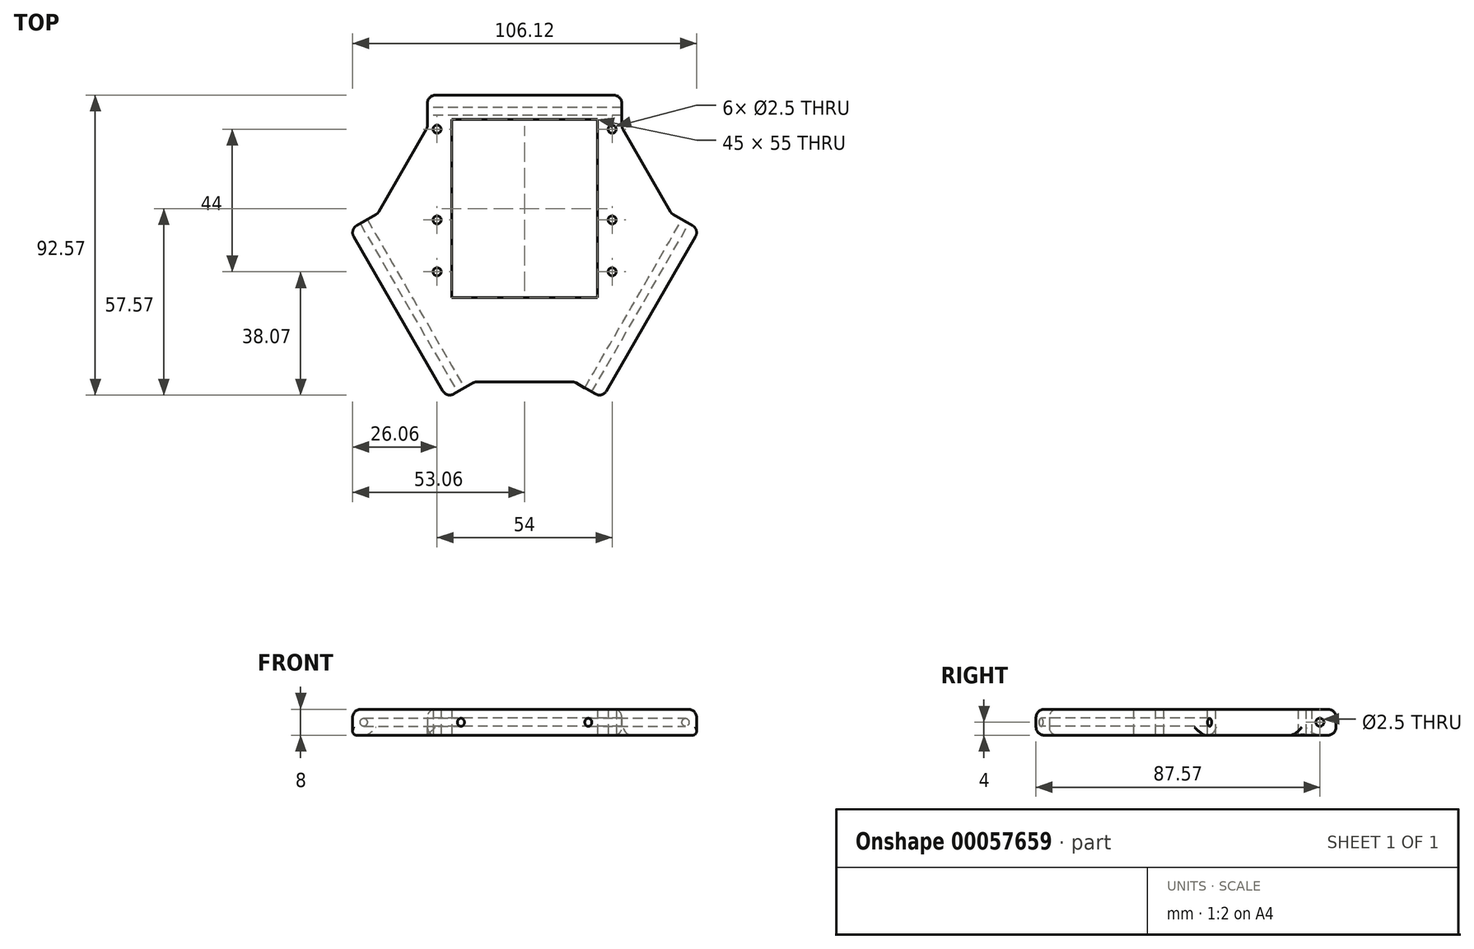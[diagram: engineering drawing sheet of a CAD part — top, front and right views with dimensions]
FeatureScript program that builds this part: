
annotation { "Feature Type Name" : "Feature", "Feature Type Description" : "" }
export const myFeature = defineFeature(function(context is Context, id is Id, definition is map)
    precondition{}
    {
        {
            var Q0;
            Q0=qCreatedBy(makeId("Top.planeOp"),FACE);
            var sketch = newSketch(context, id + "F0", { "sketchPlane" : qUnion([Q0])});
            skLineSegment(sketch, "E0", {"start": v(0, 0) * mm, "end": v(0, 78.7) * mm, "construction": true});
            skLineSegment(sketch, "E1", {"start": v(0, 0) * mm, "end": v(-104.2, -60.16) * mm, "construction": true});
            skLineSegment(sketch, "E2", {"start": v(0, 0) * mm, "end": v(103.59, -59.8) * mm, "construction": true});
            skLineSegment(sketch, "E3.bottom", {"start": v(-30, 45) * mm, "end": v(30, 45) * mm});
            skLineSegment(sketch, "E3.top", {"start": v(-30, 35) * mm, "end": v(30, 35) * mm});
            skLineSegment(sketch, "E3.left", {"start": v(-30, 45) * mm, "end": v(-30, 35) * mm});
            skLineSegment(sketch, "E3.right", {"start": v(30, 45) * mm, "end": v(30, 35) * mm});
            skPoint(sketch, "E4", {"position": v(0, 35) * mm});
            skPoint(sketch, "E5", {"position": v(0, 0) * mm});
            skLineSegment(sketch, "E6.rect.bottom", {"start": v(22.5, -17.5) * mm, "end": v(-22.5, -17.5) * mm});
            skLineSegment(sketch, "E6.rect.top", {"start": v(22.5, 17.5) * mm, "end": v(-22.5, 17.5) * mm});
            skLineSegment(sketch, "E6.rect.left", {"start": v(22.5, -17.5) * mm, "end": v(22.5, 17.5) * mm});
            skLineSegment(sketch, "E6.rect.right", {"start": v(-22.5, -17.5) * mm, "end": v(-22.5, 17.5) * mm});
            skLineSegment(sketch, "E7.1.0", {"start": v(-23.97, -48.48) * mm, "end": v(-53.97, 3.48) * mm});
            skLineSegment(sketch, "E7.1.1", {"start": v(-15.31, -43.48) * mm, "end": v(-45.31, 8.48) * mm});
            skLineSegment(sketch, "E7.1.2", {"start": v(-53.97, 3.48) * mm, "end": v(-45.31, 8.48) * mm});
            skLineSegment(sketch, "E7.1.3", {"start": v(-23.97, -48.48) * mm, "end": v(-15.31, -43.48) * mm});
            skLineSegment(sketch, "E7.2.0", {"start": v(53.97, 3.48) * mm, "end": v(23.97, -48.48) * mm});
            skLineSegment(sketch, "E7.2.1", {"start": v(45.31, 8.48) * mm, "end": v(15.31, -43.48) * mm});
            skLineSegment(sketch, "E7.2.2", {"start": v(23.97, -48.48) * mm, "end": v(15.31, -43.48) * mm});
            skLineSegment(sketch, "E7.2.3", {"start": v(53.97, 3.48) * mm, "end": v(45.31, 8.48) * mm});
            skLineSegment(sketch, "E8", {"start": v(-45.31, 8.48) * mm, "end": v(-30, 35) * mm});
            skLineSegment(sketch, "E9", {"start": v(30, 35) * mm, "end": v(45.31, 8.48) * mm});
            skLineSegment(sketch, "E10", {"start": v(15.31, -43.48) * mm, "end": v(-15.31, -43.48) * mm});
            skLineSegment(sketch, "E11.bottom", {"start": v(-22.5, 17.5) * mm, "end": v(22.5, 17.5) * mm});
            skLineSegment(sketch, "E11.top", {"start": v(-22.5, 37.5) * mm, "end": v(22.5, 37.5) * mm});
            skLineSegment(sketch, "E11.left", {"start": v(-22.5, 17.5) * mm, "end": v(-22.5, 37.5) * mm});
            skLineSegment(sketch, "E11.right", {"start": v(22.5, 17.5) * mm, "end": v(22.5, 37.5) * mm});
            skPoint(sketch, "E12", {"position": v(-27, -9.5) * mm});
            skPoint(sketch, "E13", {"position": v(-27, 6.5) * mm});
            skPoint(sketch, "E14", {"position": v(27, -9.5) * mm});
            skPoint(sketch, "E15", {"position": v(27, 6.5) * mm});
            skPoint(sketch, "E16", {"position": v(-27, 34.5) * mm});
            skPoint(sketch, "E17", {"position": v(27, 34.5) * mm});
            skLineSegment(sketch, "E18", {"start": v(-27, -9.5) * mm, "end": v(27, -9.5) * mm, "construction": true});
            skPoint(sketch, "E19", {"position": v(0, -9.5) * mm});
            skLineSegment(sketch, "E20", {"start": v(0, 0) * mm, "end": v(0, -52.67) * mm, "construction": true});
            skSolve(sketch);
        }
        {
            var Q0;
            Q0=makeQuery(id+"F0.imprint","IMPRINT",FACE,{"disambiguationData":[TD([[makeQuery(id+"F0.imprint","IMPRINT",EDGE,{"derivedFrom":sQuery(id+"F0.wireOp",EDGE,"E3.top")}),-1.0]])]});
            var Q1;
            Q1=makeQuery(id+"F0.imprint","IMPRINT",FACE,{"disambiguationData":[TD([[makeQuery(id+"F0.imprint","IMPRINT",EDGE,{"derivedFrom":sQuery(id+"F0.wireOp",EDGE,"E7.1.0")}),-1.0]])]});
            var Q2;
            Q2=makeQuery(id+"F0.imprint","IMPRINT",FACE,{"disambiguationData":[TD([[makeQuery(id+"F0.imprint","IMPRINT",EDGE,{"derivedFrom":sQuery(id+"F0.wireOp",EDGE,"E3.bottom")}),-1.0]])]});
            var Q3;
            Q3=makeQuery(id+"F0.imprint","IMPRINT",FACE,{"disambiguationData":[TD([[makeQuery(id+"F0.imprint","IMPRINT",EDGE,{"derivedFrom":sQuery(id+"F0.wireOp",EDGE,"E7.2.0")}),-1.0]])]});
            extrude(context, id + "F1", {"entities" : qUnion([Q0, Q1, Q2, Q3]), "depth" : 8 * mm});
        }
        {
            var Q0;
            Q0=makeQuery(id+"F1.opExtrude","SWEPT_FACE",FACE,{"disambiguationData":[OSD([sQuery(id+"F0.wireOp",EDGE,"E3.left")])]});
            var sketch = newSketch(context, id + "F2", { "sketchPlane" : qUnion([Q0])});
            skPoint(sketch, "E21.0", {"position": v(-45, 0) * mm});
            skPoint(sketch, "E21.1", {"position": v(-45, 8) * mm});
            skPoint(sketch, "E22", {"position": v(-40, 4) * mm});
            skSolve(sketch);
        }
        {
            var Q0;
            Q0=sQuery(id+"F2.wireOp",VERTEX,"E22");
            var Q1;
            Q1=makeQuery(id+"F1.opExtrude","SWEPT_BODY",BODY,{"disambiguationData":[OSD([sQuery(id+"F0.wireOp",EDGE,"E3.bottom"),sQuery(id+"F0.wireOp",EDGE,"E3.left"),sQuery(id+"F0.wireOp",EDGE,"E3.right"),sQuery(id+"F0.wireOp",EDGE,"E6.rect.bottom"),sQuery(id+"F0.wireOp",EDGE,"E6.rect.left"),sQuery(id+"F0.wireOp",EDGE,"E6.rect.right"),sQuery(id+"F0.wireOp",EDGE,"E7.1.0"),sQuery(id+"F0.wireOp",EDGE,"E7.1.2"),sQuery(id+"F0.wireOp",EDGE,"E7.1.3"),sQuery(id+"F0.wireOp",EDGE,"E7.2.0"),sQuery(id+"F0.wireOp",EDGE,"E7.2.2"),sQuery(id+"F0.wireOp",EDGE,"E7.2.3"),sQuery(id+"F0.wireOp",EDGE,"E8"),sQuery(id+"F0.wireOp",EDGE,"E9"),sQuery(id+"F0.wireOp",EDGE,"E10"),sQuery(id+"F0.wireOp",EDGE,"E11.top"),sQuery(id+"F0.wireOp",EDGE,"E11.left"),sQuery(id+"F0.wireOp",EDGE,"E11.right")])]});
            hole(context, id + "F3", {"style" : HoleStyle.SIMPLE, "holeDiameter" : 2.5 * mm, "endStyle" : HoleEndStyle.THROUGH, "locations" : qUnion([Q0]), "scope" : qUnion([Q1])});
        }
        {
            var Q0;
            Q0=makeQuery(id+"F1.opExtrude","SWEPT_FACE",FACE,{"disambiguationData":[OSD([sQuery(id+"F0.wireOp",EDGE,"E7.1.3")])]});
            var sketch = newSketch(context, id + "F4", { "sketchPlane" : qUnion([Q0])});
            skPoint(sketch, "E23", {"position": v(-40, 4) * mm});
            skSolve(sketch);
        }
        {
            var Q0;
            Q0=sQuery(id+"F4.wireOp",VERTEX,"E23");
            var Q1;
            Q1=makeQuery(id+"F1.opExtrude","SWEPT_BODY",BODY,{"disambiguationData":[OSD([sQuery(id+"F0.wireOp",EDGE,"E3.bottom"),sQuery(id+"F0.wireOp",EDGE,"E3.left"),sQuery(id+"F0.wireOp",EDGE,"E3.right"),sQuery(id+"F0.wireOp",EDGE,"E6.rect.bottom"),sQuery(id+"F0.wireOp",EDGE,"E6.rect.left"),sQuery(id+"F0.wireOp",EDGE,"E6.rect.right"),sQuery(id+"F0.wireOp",EDGE,"E7.1.0"),sQuery(id+"F0.wireOp",EDGE,"E7.1.2"),sQuery(id+"F0.wireOp",EDGE,"E7.1.3"),sQuery(id+"F0.wireOp",EDGE,"E7.2.0"),sQuery(id+"F0.wireOp",EDGE,"E7.2.2"),sQuery(id+"F0.wireOp",EDGE,"E7.2.3"),sQuery(id+"F0.wireOp",EDGE,"E8"),sQuery(id+"F0.wireOp",EDGE,"E9"),sQuery(id+"F0.wireOp",EDGE,"E10"),sQuery(id+"F0.wireOp",EDGE,"E11.top"),sQuery(id+"F0.wireOp",EDGE,"E11.left"),sQuery(id+"F0.wireOp",EDGE,"E11.right")])]});
            hole(context, id + "F5", {"style" : HoleStyle.SIMPLE, "holeDiameter" : 2.5 * mm, "endStyle" : HoleEndStyle.THROUGH, "locations" : qUnion([Q0]), "scope" : qUnion([Q1])});
        }
        {
            var Q0;
            Q0=makeQuery(id+"F1.opExtrude","SWEPT_FACE",FACE,{"disambiguationData":[OSD([sQuery(id+"F0.wireOp",EDGE,"E7.2.3")])]});
            var sketch = newSketch(context, id + "F6", { "sketchPlane" : qUnion([Q0])});
            skPoint(sketch, "E24", {"position": v(-40, 4) * mm});
            skSolve(sketch);
        }
        {
            var Q0;
            Q0=sQuery(id+"F6.wireOp",VERTEX,"E24");
            var Q1;
            Q1=makeQuery(id+"F1.opExtrude","SWEPT_BODY",BODY,{"disambiguationData":[OSD([sQuery(id+"F0.wireOp",EDGE,"E3.bottom"),sQuery(id+"F0.wireOp",EDGE,"E3.left"),sQuery(id+"F0.wireOp",EDGE,"E3.right"),sQuery(id+"F0.wireOp",EDGE,"E6.rect.bottom"),sQuery(id+"F0.wireOp",EDGE,"E6.rect.left"),sQuery(id+"F0.wireOp",EDGE,"E6.rect.right"),sQuery(id+"F0.wireOp",EDGE,"E7.1.0"),sQuery(id+"F0.wireOp",EDGE,"E7.1.2"),sQuery(id+"F0.wireOp",EDGE,"E7.1.3"),sQuery(id+"F0.wireOp",EDGE,"E7.2.0"),sQuery(id+"F0.wireOp",EDGE,"E7.2.2"),sQuery(id+"F0.wireOp",EDGE,"E7.2.3"),sQuery(id+"F0.wireOp",EDGE,"E8"),sQuery(id+"F0.wireOp",EDGE,"E9"),sQuery(id+"F0.wireOp",EDGE,"E10"),sQuery(id+"F0.wireOp",EDGE,"E11.top"),sQuery(id+"F0.wireOp",EDGE,"E11.left"),sQuery(id+"F0.wireOp",EDGE,"E11.right")])]});
            hole(context, id + "F7", {"style" : HoleStyle.SIMPLE, "holeDiameter" : 2.5 * mm, "endStyle" : HoleEndStyle.THROUGH, "locations" : qUnion([Q0]), "scope" : qUnion([Q1])});
        }
        {
            var Q0;
            Q0=makeQuery(id+"F1.opExtrude","CAP_EDGE",EDGE,{"disambiguationData":[OSD([sQuery(id+"F0.wireOp",EDGE,"E8")])],"isStart":false});
            var Q1;
            Q1=makeQuery(id+"F1.opExtrude","CAP_EDGE",EDGE,{"disambiguationData":[OSD([sQuery(id+"F0.wireOp",EDGE,"E3.left")])],"isStart":false});
            var Q2;
            Q2=makeQuery(id+"F1.opExtrude","CAP_EDGE",EDGE,{"disambiguationData":[OSD([sQuery(id+"F0.wireOp",EDGE,"E3.bottom")])],"isStart":false});
            var Q3;
            Q3=makeQuery(id+"F1.opExtrude","CAP_EDGE",EDGE,{"disambiguationData":[OSD([sQuery(id+"F0.wireOp",EDGE,"E9")])],"isStart":false});
            var Q4;
            Q4=makeQuery(id+"F1.opExtrude","CAP_EDGE",EDGE,{"disambiguationData":[OSD([sQuery(id+"F0.wireOp",EDGE,"E3.right")])],"isStart":false});
            var Q5;
            Q5=makeQuery(id+"F1.opExtrude","CAP_EDGE",EDGE,{"disambiguationData":[OSD([sQuery(id+"F0.wireOp",EDGE,"E7.2.3")])],"isStart":false});
            var Q6;
            Q6=makeQuery(id+"F1.opExtrude","CAP_EDGE",EDGE,{"disambiguationData":[OSD([sQuery(id+"F0.wireOp",EDGE,"E7.2.0")])],"isStart":false});
            var Q7;
            Q7=makeQuery(id+"F1.opExtrude","CAP_EDGE",EDGE,{"disambiguationData":[OSD([sQuery(id+"F0.wireOp",EDGE,"E7.2.2")])],"isStart":false});
            var Q8;
            Q8=makeQuery(id+"F1.opExtrude","CAP_EDGE",EDGE,{"disambiguationData":[OSD([sQuery(id+"F0.wireOp",EDGE,"E10")])],"isStart":false});
            var Q9;
            Q9=makeQuery(id+"F1.opExtrude","CAP_EDGE",EDGE,{"disambiguationData":[OSD([sQuery(id+"F0.wireOp",EDGE,"E7.1.3")])],"isStart":false});
            var Q10;
            Q10=makeQuery(id+"F1.opExtrude","CAP_EDGE",EDGE,{"disambiguationData":[OSD([sQuery(id+"F0.wireOp",EDGE,"E7.1.0")])],"isStart":false});
            var Q11;
            Q11=makeQuery(id+"F1.opExtrude","CAP_EDGE",EDGE,{"disambiguationData":[OSD([sQuery(id+"F0.wireOp",EDGE,"E7.1.2")])],"isStart":false});
            var Q12;
            Q12=makeQuery(id+"F1.opExtrude","SWEPT_EDGE",EDGE,{"disambiguationData":[OSD([sQuery(id+"F0.wireOp",EDGE,"E7.1.0"),sQuery(id+"F0.wireOp",EDGE,"E7.1.2")])]});
            var Q13;
            Q13=makeQuery(id+"F1.opExtrude","SWEPT_EDGE",EDGE,{"disambiguationData":[OSD([sQuery(id+"F0.wireOp",EDGE,"E7.1.1"),sQuery(id+"F0.wireOp",EDGE,"E7.1.2"),sQuery(id+"F0.wireOp",EDGE,"E8")])]});
            var Q14;
            Q14=makeQuery(id+"F1.opExtrude","SWEPT_EDGE",EDGE,{"disambiguationData":[OSD([sQuery(id+"F0.wireOp",EDGE,"E3.top"),sQuery(id+"F0.wireOp",EDGE,"E3.left"),sQuery(id+"F0.wireOp",EDGE,"E8")])]});
            var Q15;
            Q15=makeQuery(id+"F1.opExtrude","SWEPT_EDGE",EDGE,{"disambiguationData":[OSD([sQuery(id+"F0.wireOp",EDGE,"E3.bottom"),sQuery(id+"F0.wireOp",EDGE,"E3.left")])]});
            var Q16;
            Q16=makeQuery(id+"F1.opExtrude","SWEPT_EDGE",EDGE,{"disambiguationData":[OSD([sQuery(id+"F0.wireOp",EDGE,"E3.bottom"),sQuery(id+"F0.wireOp",EDGE,"E3.right")])]});
            var Q17;
            Q17=makeQuery(id+"F1.opExtrude","SWEPT_EDGE",EDGE,{"disambiguationData":[OSD([sQuery(id+"F0.wireOp",EDGE,"E3.top"),sQuery(id+"F0.wireOp",EDGE,"E3.right"),sQuery(id+"F0.wireOp",EDGE,"E9")])]});
            var Q18;
            Q18=makeQuery(id+"F1.opExtrude","SWEPT_EDGE",EDGE,{"disambiguationData":[OSD([sQuery(id+"F0.wireOp",EDGE,"E7.2.1"),sQuery(id+"F0.wireOp",EDGE,"E7.2.3"),sQuery(id+"F0.wireOp",EDGE,"E9")])]});
            var Q19;
            Q19=makeQuery(id+"F1.opExtrude","SWEPT_EDGE",EDGE,{"disambiguationData":[OSD([sQuery(id+"F0.wireOp",EDGE,"E7.2.0"),sQuery(id+"F0.wireOp",EDGE,"E7.2.3")])]});
            var Q20;
            Q20=makeQuery(id+"F1.opExtrude","SWEPT_EDGE",EDGE,{"disambiguationData":[OSD([sQuery(id+"F0.wireOp",EDGE,"E7.2.0"),sQuery(id+"F0.wireOp",EDGE,"E7.2.2")])]});
            var Q21;
            Q21=makeQuery(id+"F1.opExtrude","SWEPT_EDGE",EDGE,{"disambiguationData":[OSD([sQuery(id+"F0.wireOp",EDGE,"E7.2.1"),sQuery(id+"F0.wireOp",EDGE,"E7.2.2"),sQuery(id+"F0.wireOp",EDGE,"E10")])]});
            var Q22;
            Q22=makeQuery(id+"F1.opExtrude","SWEPT_EDGE",EDGE,{"disambiguationData":[OSD([sQuery(id+"F0.wireOp",EDGE,"E7.1.1"),sQuery(id+"F0.wireOp",EDGE,"E7.1.3"),sQuery(id+"F0.wireOp",EDGE,"E10")])]});
            var Q23;
            Q23=makeQuery(id+"F1.opExtrude","SWEPT_EDGE",EDGE,{"disambiguationData":[OSD([sQuery(id+"F0.wireOp",EDGE,"E7.1.0"),sQuery(id+"F0.wireOp",EDGE,"E7.1.3")])]});
            var Q24;
            Q24=makeQuery(id+"F1.opExtrude","CAP_EDGE",EDGE,{"disambiguationData":[OSD([sQuery(id+"F0.wireOp",EDGE,"E7.1.0")])],"isStart":true});
            var Q25;
            Q25=makeQuery(id+"F1.opExtrude","CAP_EDGE",EDGE,{"disambiguationData":[OSD([sQuery(id+"F0.wireOp",EDGE,"E8")])],"isStart":true});
            var Q26;
            Q26=makeQuery(id+"F1.opExtrude","SWEPT_FACE",FACE,{"disambiguationData":[OSD([sQuery(id+"F0.wireOp",EDGE,"E3.bottom")])]});
            var Q27;
            Q27=makeQuery(id+"F1.opExtrude","CAP_EDGE",EDGE,{"disambiguationData":[OSD([sQuery(id+"F0.wireOp",EDGE,"E3.right")])],"isStart":true});
            var Q28;
            Q28=makeQuery(id+"F1.opExtrude","CAP_EDGE",EDGE,{"disambiguationData":[OSD([sQuery(id+"F0.wireOp",EDGE,"E7.2.0")])],"isStart":true});
            var Q29;
            Q29=makeQuery(id+"F1.opExtrude","CAP_EDGE",EDGE,{"disambiguationData":[OSD([sQuery(id+"F0.wireOp",EDGE,"E7.2.2")])],"isStart":true});
            var Q30;
            Q30=makeQuery(id+"F1.opExtrude","CAP_EDGE",EDGE,{"disambiguationData":[OSD([sQuery(id+"F0.wireOp",EDGE,"E10")])],"isStart":true});
            var Q31;
            Q31=makeQuery(id+"F1.opExtrude","CAP_EDGE",EDGE,{"disambiguationData":[OSD([sQuery(id+"F0.wireOp",EDGE,"E7.1.3")])],"isStart":true});
            fillet(context, id + "F8", {"entities" : qUnion([Q0, Q1, Q2, Q3, Q4, Q5, Q6, Q7, Q8, Q9, Q10, Q11, Q12, Q13, Q14, Q15, Q16, Q17, Q18, Q19, Q20, Q21, Q22, Q23, Q24, Q25, Q26, Q27, Q28, Q29, Q30, Q31]), "radius" : 2.5 * mm, "tangentPropagation" : true, "allowEdgeOverflow" : false});
        }
        {
            var Q0;
            Q0=sQuery(id+"F0.wireOp",VERTEX,"E13");
            var Q1;
            Q1=sQuery(id+"F0.wireOp",VERTEX,"E12");
            var Q2;
            Q2=sQuery(id+"F0.wireOp",VERTEX,"E14");
            var Q3;
            Q3=sQuery(id+"F0.wireOp",VERTEX,"E15");
            var Q4;
            Q4=sQuery(id+"F0.wireOp",VERTEX,"E16");
            var Q5;
            Q5=sQuery(id+"F0.wireOp",VERTEX,"E17");
            var Q6;
            Q6=makeQuery(id+"F1.opExtrude","SWEPT_BODY",BODY,{"disambiguationData":[OSD([sQuery(id+"F0.wireOp",EDGE,"E3.bottom"),sQuery(id+"F0.wireOp",EDGE,"E3.left"),sQuery(id+"F0.wireOp",EDGE,"E3.right"),sQuery(id+"F0.wireOp",EDGE,"E6.rect.bottom"),sQuery(id+"F0.wireOp",EDGE,"E6.rect.left"),sQuery(id+"F0.wireOp",EDGE,"E6.rect.right"),sQuery(id+"F0.wireOp",EDGE,"E7.1.0"),sQuery(id+"F0.wireOp",EDGE,"E7.1.2"),sQuery(id+"F0.wireOp",EDGE,"E7.1.3"),sQuery(id+"F0.wireOp",EDGE,"E7.2.0"),sQuery(id+"F0.wireOp",EDGE,"E7.2.2"),sQuery(id+"F0.wireOp",EDGE,"E7.2.3"),sQuery(id+"F0.wireOp",EDGE,"E8"),sQuery(id+"F0.wireOp",EDGE,"E9"),sQuery(id+"F0.wireOp",EDGE,"E10"),sQuery(id+"F0.wireOp",EDGE,"E11.top"),sQuery(id+"F0.wireOp",EDGE,"E11.left"),sQuery(id+"F0.wireOp",EDGE,"E11.right")])]});
            hole(context, id + "F9", {"style" : HoleStyle.SIMPLE, "holeDiameter" : 2.5 * mm, "endStyle" : HoleEndStyle.THROUGH, "oppositeDirection" : true, "locations" : qUnion([Q0, Q1, Q2, Q3, Q4, Q5]), "scope" : qUnion([Q6])});
        }
    });
